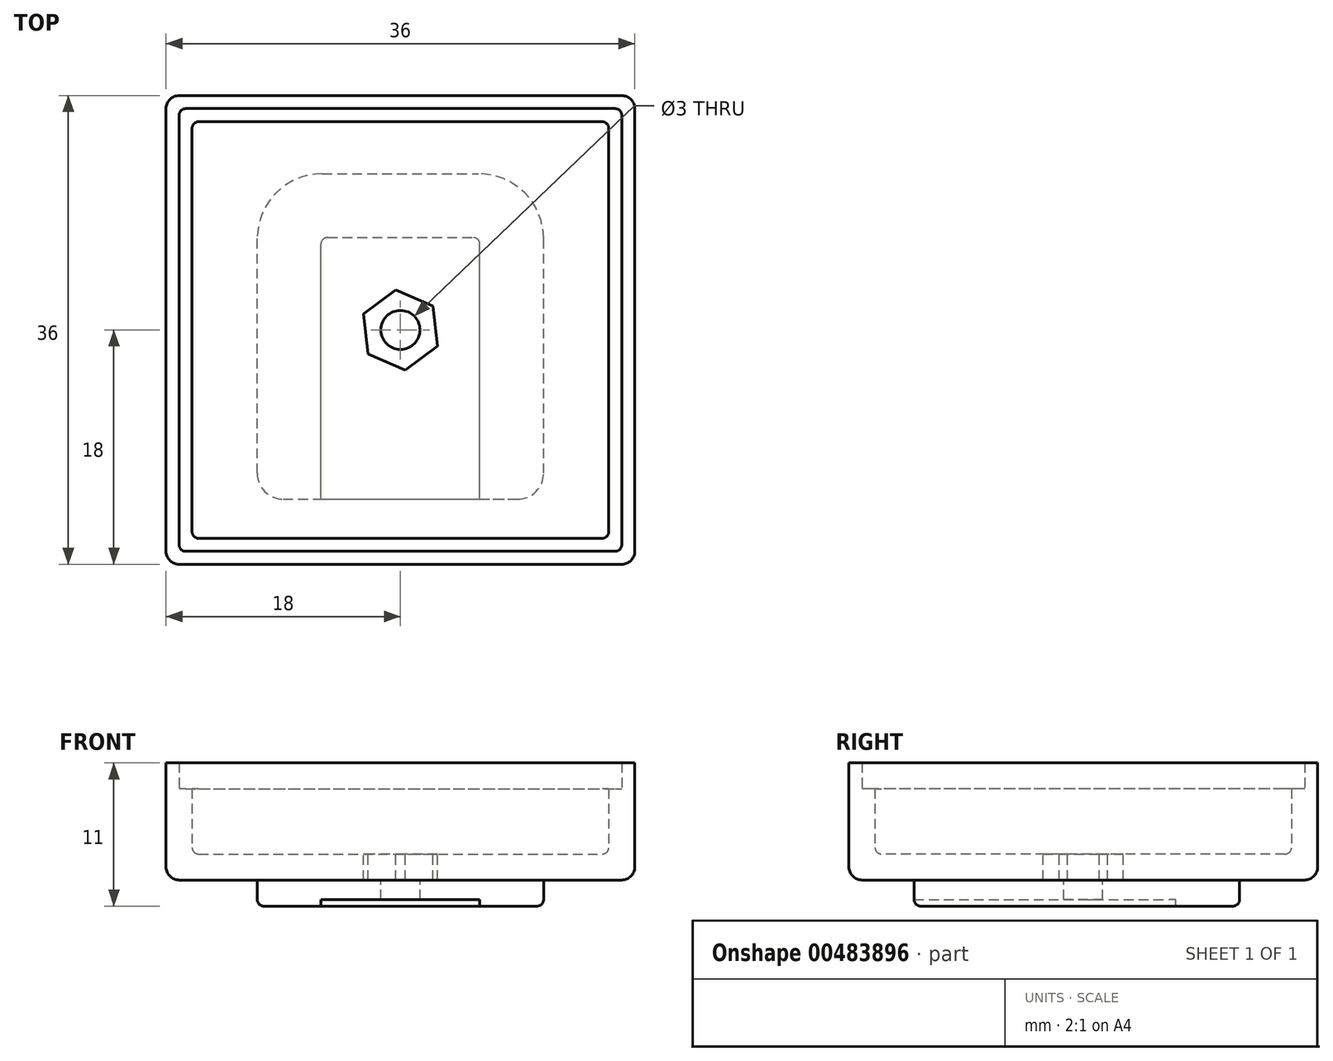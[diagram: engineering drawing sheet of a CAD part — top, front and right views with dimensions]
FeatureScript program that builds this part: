
annotation { "Feature Type Name" : "Feature", "Feature Type Description" : "" }
export const myFeature = defineFeature(function(context is Context, id is Id, definition is map)
    precondition{}
    {
        {
            var Q0;
            Q0=qCreatedBy(makeId("Top.planeOp"),FACE);
            var sketch = newSketch(context, id + "F0", { "sketchPlane" : qUnion([Q0])});
            skLineSegment(sketch, "E0.bottom", {"start": v(-17, 17) * mm, "end": v(17, 17) * mm});
            skLineSegment(sketch, "E0.top", {"start": v(-17, -17) * mm, "end": v(17, -17) * mm});
            skLineSegment(sketch, "E0.left", {"start": v(-17, 17) * mm, "end": v(-17, -17) * mm});
            skLineSegment(sketch, "E0.right", {"start": v(17, 17) * mm, "end": v(17, -17) * mm});
            skSolve(sketch);
        }
        {
            var Q0;
            Q0=qCreatedBy(makeId("Top.planeOp"),FACE);
            var sketch = newSketch(context, id + "F1", { "sketchPlane" : qUnion([Q0])});
            skLineSegment(sketch, "E1.bottom", {"start": v(-18, 18) * mm, "end": v(18, 18) * mm});
            skLineSegment(sketch, "E1.top", {"start": v(-18, -18) * mm, "end": v(18, -18) * mm});
            skLineSegment(sketch, "E1.left", {"start": v(-18, 18) * mm, "end": v(-18, -18) * mm});
            skLineSegment(sketch, "E1.right", {"start": v(18, 18) * mm, "end": v(18, -18) * mm});
            skSolve(sketch);
        }
        {
            var Q0;
            Q0=makeQuery(id+"F1.imprint","IMPRINT",FACE,{"disambiguationData":[TD([[makeQuery(id+"F1.imprint","IMPRINT",EDGE,{"derivedFrom":sQuery(id+"F1.wireOp",EDGE,"E1.bottom")}),-1.0]])]});
            extrude(context, id + "F2", {"entities" : qUnion([Q0]), "depth" : 9 * mm});
        }
        {
            var Q0;
            Q0=makeQuery(id+"F2.opExtrude","CAP_FACE",FACE,{"disambiguationData":[OSD([sQuery(id+"F1.wireOp",EDGE,"E1.bottom"),sQuery(id+"F1.wireOp",EDGE,"E1.top"),sQuery(id+"F1.wireOp",EDGE,"E1.left"),sQuery(id+"F1.wireOp",EDGE,"E1.right")])],"isStart":false});
            shell(context, id + "F3", {"entities" : qUnion([Q0]), "thickness" : 2 * mm});
        }
        {
            var Q0;
            Q0=makeQuery(id+"F0.imprint","IMPRINT",FACE,{"disambiguationData":[TD([[makeQuery(id+"F0.imprint","IMPRINT",EDGE,{"derivedFrom":sQuery(id+"F0.wireOp",EDGE,"E0.bottom")}),-1.0]])]});
            extrude(context, id + "F4", {"entities" : qUnion([Q0]), "operationType" : NewBodyOperationType.REMOVE, "depth" : 10 * mm, "hasSecondDirection" : true, "secondDirectionOppositeDirection" : true, "secondDirectionDepth" : -7 * mm});
        }
        {
            var Q0;
            Q0=makeQuery(id+"F2.opExtrude","CAP_EDGE",EDGE,{"disambiguationData":[OSD([sQuery(id+"F1.wireOp",EDGE,"E1.right")])],"isStart":true});
            var Q1;
            Q1=makeQuery(id+"F2.opExtrude","CAP_EDGE",EDGE,{"disambiguationData":[OSD([sQuery(id+"F1.wireOp",EDGE,"E1.bottom")])],"isStart":true});
            var Q2;
            Q2=makeQuery(id+"F2.opExtrude","CAP_EDGE",EDGE,{"disambiguationData":[OSD([sQuery(id+"F1.wireOp",EDGE,"E1.left")])],"isStart":true});
            var Q3;
            Q3=makeQuery(id+"F2.opExtrude","CAP_EDGE",EDGE,{"disambiguationData":[OSD([sQuery(id+"F1.wireOp",EDGE,"E1.top")])],"isStart":true});
            fillet(context, id + "F5", {"entities" : qUnion([Q0, Q1, Q2, Q3]), "radius" : 1 * mm, "tangentPropagation" : true, "allowEdgeOverflow" : false});
        }
        {
            var Q0;
            Q0=makeQuery(id+"F3.opShell","OFFSET_FACE",FACE,{"disambiguationData":[OSD([sQuery(id+"F1.wireOp",EDGE,"E1.bottom"),sQuery(id+"F1.wireOp",EDGE,"E1.top"),sQuery(id+"F1.wireOp",EDGE,"E1.left"),sQuery(id+"F1.wireOp",EDGE,"E1.right")])]});
            var Q1;
            Q1=makeQuery(id+"F3.opShell","OFFSET_EDGE",EDGE,{"disambiguationData":[OSD([sQuery(id+"F1.wireOp",EDGE,"E1.bottom"),sQuery(id+"F1.wireOp",EDGE,"E1.left")])]});
            var Q2;
            Q2=makeQuery(id+"F3.opShell","OFFSET_EDGE",EDGE,{"disambiguationData":[OSD([sQuery(id+"F1.wireOp",EDGE,"E1.bottom"),sQuery(id+"F1.wireOp",EDGE,"E1.right")])]});
            var Q3;
            Q3=makeQuery(id+"F4.boolean.opBoolean","COPY",EDGE,{"derivedFrom":makeQuery(id+"F4.opExtrude","SWEPT_EDGE",EDGE,{"disambiguationData":[OSD([sQuery(id+"F0.wireOp",EDGE,"E0.bottom"),sQuery(id+"F0.wireOp",EDGE,"E0.right")])]})});
            var Q4;
            Q4=makeQuery(id+"F4.boolean.opBoolean","COPY",EDGE,{"derivedFrom":makeQuery(id+"F4.opExtrude","SWEPT_EDGE",EDGE,{"disambiguationData":[OSD([sQuery(id+"F0.wireOp",EDGE,"E0.top"),sQuery(id+"F0.wireOp",EDGE,"E0.right")])]})});
            var Q5;
            Q5=makeQuery(id+"F3.opShell","OFFSET_EDGE",EDGE,{"disambiguationData":[OSD([sQuery(id+"F1.wireOp",EDGE,"E1.top"),sQuery(id+"F1.wireOp",EDGE,"E1.right")])]});
            var Q6;
            Q6=makeQuery(id+"F4.boolean.opBoolean","COPY",EDGE,{"derivedFrom":makeQuery(id+"F4.opExtrude","SWEPT_EDGE",EDGE,{"disambiguationData":[OSD([sQuery(id+"F0.wireOp",EDGE,"E0.top"),sQuery(id+"F0.wireOp",EDGE,"E0.left")])]})});
            var Q7;
            Q7=makeQuery(id+"F3.opShell","OFFSET_EDGE",EDGE,{"disambiguationData":[OSD([sQuery(id+"F1.wireOp",EDGE,"E1.top"),sQuery(id+"F1.wireOp",EDGE,"E1.left")])]});
            var Q8;
            Q8=makeQuery(id+"F4.boolean.opBoolean","COPY",EDGE,{"derivedFrom":makeQuery(id+"F4.opExtrude","SWEPT_EDGE",EDGE,{"disambiguationData":[OSD([sQuery(id+"F0.wireOp",EDGE,"E0.bottom"),sQuery(id+"F0.wireOp",EDGE,"E0.left")])]})});
            fillet(context, id + "F6", {"entities" : qUnion([Q0, Q1, Q2, Q3, Q4, Q5, Q6, Q7, Q8]), "radius" : 0.5 * mm, "tangentPropagation" : true, "allowEdgeOverflow" : false});
        }
        {
            var Q0;
            Q0=makeQuery(id+"F2.opExtrude","SWEPT_EDGE",EDGE,{"disambiguationData":[OSD([sQuery(id+"F1.wireOp",EDGE,"E1.top"),sQuery(id+"F1.wireOp",EDGE,"E1.left")])]});
            var Q1;
            Q1=makeQuery(id+"F2.opExtrude","SWEPT_EDGE",EDGE,{"disambiguationData":[OSD([sQuery(id+"F1.wireOp",EDGE,"E1.bottom"),sQuery(id+"F1.wireOp",EDGE,"E1.right")])]});
            var Q2;
            Q2=makeQuery(id+"F2.opExtrude","SWEPT_EDGE",EDGE,{"disambiguationData":[OSD([sQuery(id+"F1.wireOp",EDGE,"E1.top"),sQuery(id+"F1.wireOp",EDGE,"E1.right")])]});
            var Q3;
            Q3=makeQuery(id+"F2.opExtrude","SWEPT_EDGE",EDGE,{"disambiguationData":[OSD([sQuery(id+"F1.wireOp",EDGE,"E1.bottom"),sQuery(id+"F1.wireOp",EDGE,"E1.left")])]});
            fillet(context, id + "F7", {"entities" : qUnion([Q0, Q1, Q2, Q3]), "radius" : 1 * mm, "tangentPropagation" : true, "allowEdgeOverflow" : false});
        }
        {
            var Q0;
            Q0=qCreatedBy(makeId("Top.planeOp"),FACE);
            var sketch = newSketch(context, id + "F8", { "sketchPlane" : qUnion([Q0])});
            skLineSegment(sketch, "E2.bottom", {"start": v(-9, -13) * mm, "end": v(9, -13) * mm});
            skLineSegment(sketch, "E2.top", {"start": v(-6, 12) * mm, "end": v(6, 12) * mm});
            skLineSegment(sketch, "E2.left", {"start": v(-11, -11) * mm, "end": v(-11, 7) * mm});
            skLineSegment(sketch, "E2.right", {"start": v(11, -11) * mm, "end": v(11, 7) * mm});
            skPoint(sketch, "E3.visualSharp", {"position": v(-11, 12) * mm});
            skArc(sketch, "E3.filletArc", {"start": v(-6, 12) * mm, "mid": v(-9.54, 10.54) * mm, "end": v(-11, 7) * mm});
            skPoint(sketch, "E4.visualSharp", {"position": v(11, 12) * mm});
            skArc(sketch, "E4.filletArc", {"start": v(11, 7) * mm, "mid": v(9.54, 10.54) * mm, "end": v(6, 12) * mm});
            skPoint(sketch, "E5.visualSharp", {"position": v(-11, -13) * mm});
            skArc(sketch, "E5.filletArc", {"start": v(-11, -11) * mm, "mid": v(-10.41, -12.41) * mm, "end": v(-9, -13) * mm});
            skPoint(sketch, "E6.visualSharp", {"position": v(11, -13) * mm});
            skArc(sketch, "E6.filletArc", {"start": v(9, -13) * mm, "mid": v(10.41, -12.41) * mm, "end": v(11, -11) * mm});
            skSolve(sketch);
        }
        {
            var Q0;
            Q0 = qSketchRegion(id + "F8", true);
            extrude(context, id + "F9", {"entities" : qUnion([Q0]), "operationType" : NewBodyOperationType.ADD, "oppositeDirection" : true, "depth" : 2 * mm});
        }
        {
            var Q0;
            Q0=qCreatedBy(makeId("Top.planeOp"),FACE);
            var sketch = newSketch(context, id + "F10", { "sketchPlane" : qUnion([Q0])});
            skLineSegment(sketch, "E7.bottom", {"start": v(-6.1, -13) * mm, "end": v(6.1, -13) * mm});
            skLineSegment(sketch, "E7.top", {"start": v(-6.1, 7.1) * mm, "end": v(6.1, 7.1) * mm});
            skLineSegment(sketch, "E7.left", {"start": v(-6.1, -13) * mm, "end": v(-6.1, 7.1) * mm});
            skLineSegment(sketch, "E7.right", {"start": v(6.1, -13) * mm, "end": v(6.1, 7.1) * mm});
            skSolve(sketch);
        }
        {
            var Q0;
            Q0 = qSketchRegion(id + "F10", true);
            extrude(context, id + "F11", {"entities" : qUnion([Q0]), "operationType" : NewBodyOperationType.REMOVE, "oppositeDirection" : true, "depth" : 4 * mm, "hasSecondDirection" : true, "secondDirectionOppositeDirection" : true, "secondDirectionDepth" : 1.5 * mm});
        }
        {
            var Q0;
            Q0=makeQuery(id+"F3.opShell","OFFSET_FACE",FACE,{"disambiguationData":[OSD([sQuery(id+"F1.wireOp",EDGE,"E1.bottom"),sQuery(id+"F1.wireOp",EDGE,"E1.top"),sQuery(id+"F1.wireOp",EDGE,"E1.left"),sQuery(id+"F1.wireOp",EDGE,"E1.right")])]});
            var sketch = newSketch(context, id + "F12", { "sketchPlane" : qUnion([Q0])});
            skCircle(sketch, "E8.cCircle", {"center": v(0, 0) * mm, "radius": 3.1 * mm, "construction": true});
            skLineSegment(sketch, "E8.0", {"start": v(-2.85, 1.23) * mm, "end": v(-0.36, 3.08) * mm});
            skLineSegment(sketch, "E8.1", {"start": v(-0.36, 3.08) * mm, "end": v(2.49, 1.85) * mm});
            skLineSegment(sketch, "E8.2", {"start": v(2.49, 1.85) * mm, "end": v(2.85, -1.23) * mm});
            skLineSegment(sketch, "E8.3", {"start": v(2.85, -1.23) * mm, "end": v(0.36, -3.08) * mm});
            skLineSegment(sketch, "E8.4", {"start": v(0.36, -3.08) * mm, "end": v(-2.49, -1.85) * mm});
            skLineSegment(sketch, "E8.5", {"start": v(-2.49, -1.85) * mm, "end": v(-2.85, 1.23) * mm});
            skSolve(sketch);
        }
        {
            var Q0;
            Q0=makeQuery(id+"F12.imprint","IMPRINT",FACE,{"disambiguationData":[TD([[makeQuery(id+"F12.imprint","IMPRINT",EDGE,{"derivedFrom":sQuery(id+"F12.wireOp",EDGE,"E8.0")}),-1.0]])]});
            extrude(context, id + "F13", {"entities" : qUnion([Q0]), "operationType" : NewBodyOperationType.REMOVE, "oppositeDirection" : true, "depth" : 2 * mm});
        }
        {
            var Q0;
            Q0=makeQuery(id+"F3.opShell","OFFSET_FACE",FACE,{"disambiguationData":[OSD([sQuery(id+"F1.wireOp",EDGE,"E1.bottom"),sQuery(id+"F1.wireOp",EDGE,"E1.top"),sQuery(id+"F1.wireOp",EDGE,"E1.left"),sQuery(id+"F1.wireOp",EDGE,"E1.right")])]});
            var sketch = newSketch(context, id + "F14", { "sketchPlane" : qUnion([Q0])});
            skCircle(sketch, "E9", {"center": v(0, 0) * mm, "radius": 1.5 * mm});
            skSolve(sketch);
        }
        {
            var Q0;
            Q0=makeQuery(id+"F14.imprint","IMPRINT",FACE,{"disambiguationData":[TD([[makeQuery(id+"F14.imprint","IMPRINT",EDGE,{"derivedFrom":sQuery(id+"F14.wireOp",EDGE,"E9")}),1.0]])]});
            extrude(context, id + "F15", {"entities" : qUnion([Q0]), "operationType" : NewBodyOperationType.REMOVE, "endBound" : BoundingType.THROUGH_ALL, "oppositeDirection" : true, "depth" : 25 * mm});
        }
        {
            var Q0;
            Q0=makeQuery(id+"F9.opExtrude","CAP_EDGE",EDGE,{"disambiguationData":[OSD([sQuery(id+"F8.wireOp",EDGE,"E2.right")])],"isStart":true});
            var Q1;
            Q1=makeQuery(id+"F11.boolean.opBoolean","COPY",EDGE,{"derivedFrom":makeQuery(id+"F11.opExtrude","SWEPT_EDGE",EDGE,{"disambiguationData":[OSD([sQuery(id+"F10.wireOp",EDGE,"E7.top"),sQuery(id+"F10.wireOp",EDGE,"E7.right")])]})});
            var Q2;
            Q2=makeQuery(id+"F11.boolean.opBoolean","COPY",EDGE,{"derivedFrom":makeQuery(id+"F11.opExtrude","SWEPT_EDGE",EDGE,{"disambiguationData":[OSD([sQuery(id+"F10.wireOp",EDGE,"E7.top"),sQuery(id+"F10.wireOp",EDGE,"E7.left")])]})});
            fillet(context, id + "F16", {"entities" : qUnion([Q0, Q1, Q2]), "radius" : 0.5 * mm, "tangentPropagation" : true, "allowEdgeOverflow" : false});
        }
        {
            var Q0;
            {var subQ0=sQuery(id+"F8.wireOp",EDGE,"E2.bottom");var subQ1=sQuery(id+"F8.wireOp",EDGE,"E6.filletArc");Q0=makeQuery(id+"F11.boolean.opBoolean","SPLIT",EDGE,{"disambiguationData":[TD([makeQuery(id+"F9.opExtrude","SWEPT_FACE",FACE,{"disambiguationData":[OSD([subQ1])]})])],"derivedFrom":makeQuery(id+"F9.opExtrude","CAP_EDGE",EDGE,{"disambiguationData":[OSD([subQ0])],"isStart":false})});}
            fillet(context, id + "F17", {"entities" : qUnion([Q0]), "radius" : 0.5 * mm, "tangentPropagation" : true, "allowEdgeOverflow" : false});
        }
    });
